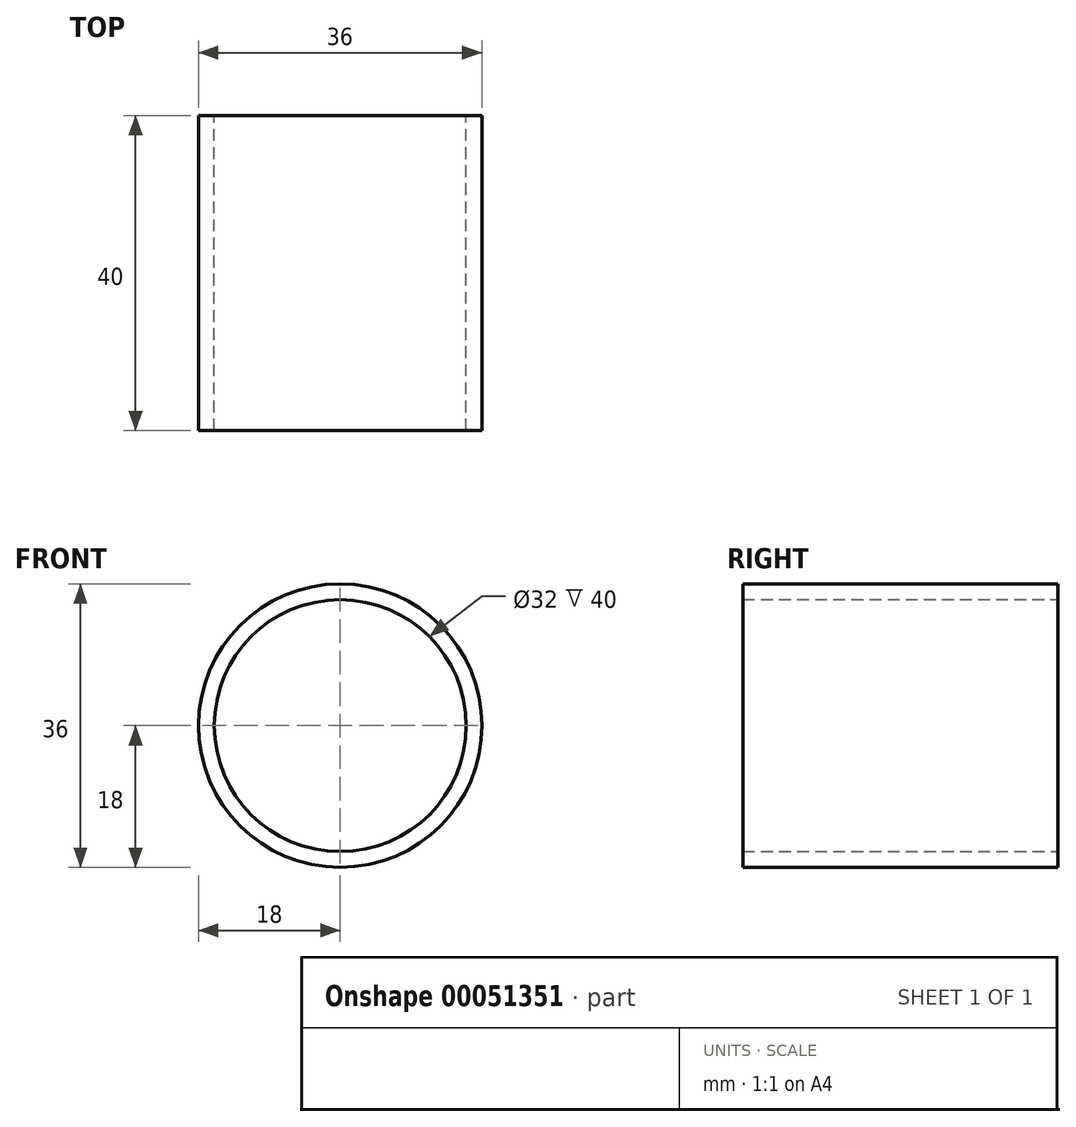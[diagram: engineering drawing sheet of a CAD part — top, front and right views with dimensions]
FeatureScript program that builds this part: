
annotation { "Feature Type Name" : "Feature", "Feature Type Description" : "" }
export const myFeature = defineFeature(function(context is Context, id is Id, definition is map)
    precondition{}
    {
        {
            var Q0;
            Q0=qCreatedBy(makeId("Front.planeOp"),FACE);
            var sketch = newSketch(context, id + "F0", { "sketchPlane" : qUnion([Q0])});
            skCircle(sketch, "E0", {"center": v(0, 0) * mm, "radius": 18 * mm});
            skCircle(sketch, "E1", {"center": v(0, 0) * mm, "radius": 16 * mm});
            skSolve(sketch);
        }
        {
            var Q0;
            Q0 = qSketchRegion(id + "F0", true);
            extrude(context, id + "F1", {"entities" : qUnion([Q0]), "depth" : (50.5 - 6 - 4.5) * mm, "symmetric" : true});
        }
    });
